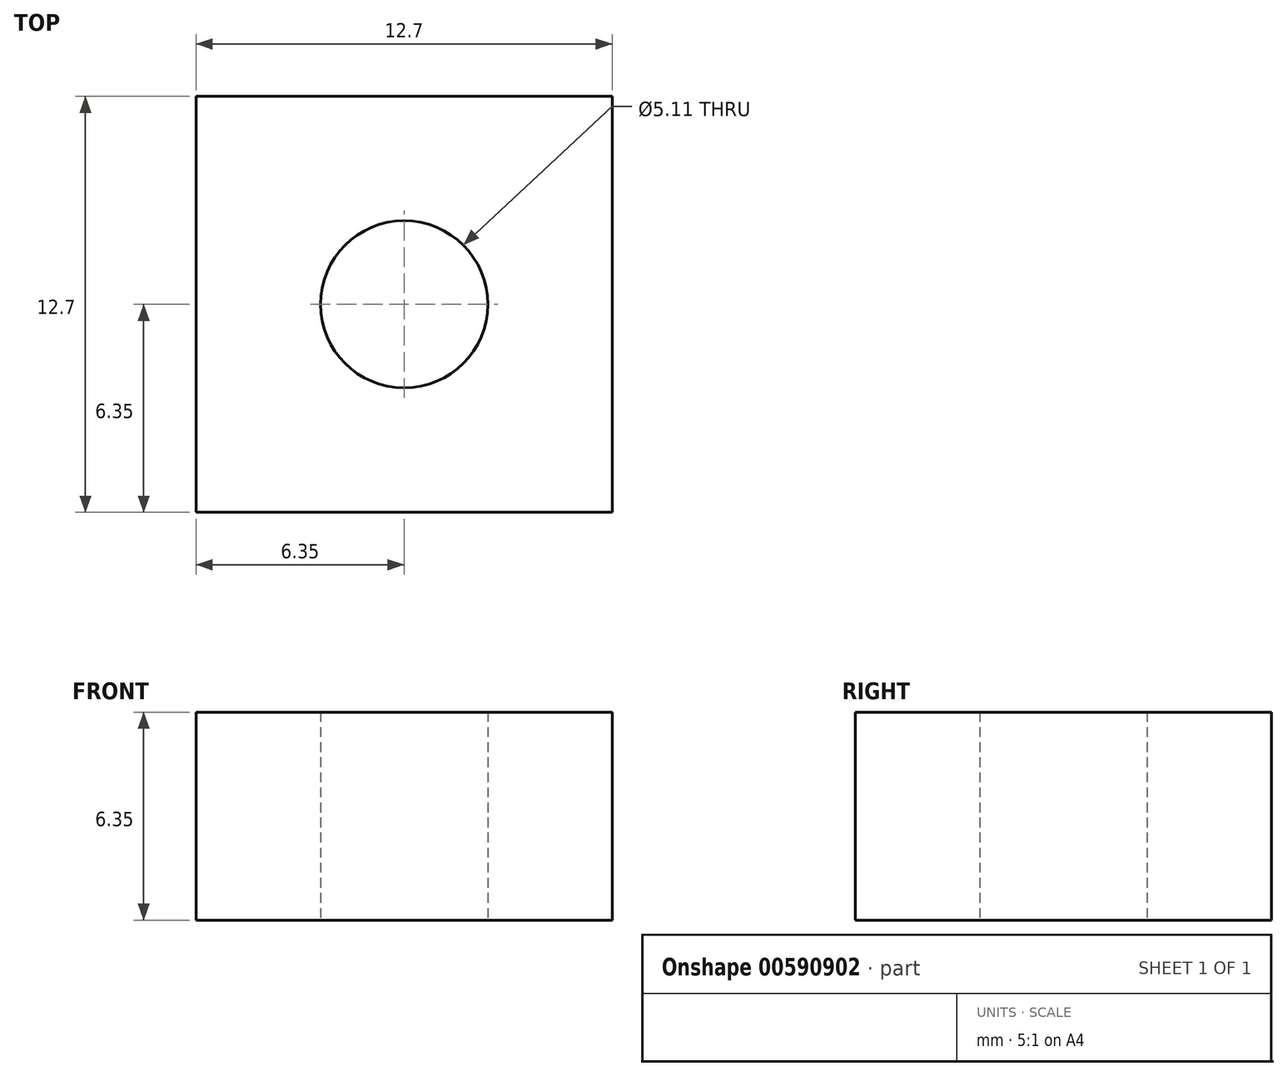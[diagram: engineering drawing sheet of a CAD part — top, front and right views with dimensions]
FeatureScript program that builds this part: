
annotation { "Feature Type Name" : "Feature", "Feature Type Description" : "" }
export const myFeature = defineFeature(function(context is Context, id is Id, definition is map)
    precondition{}
    {
        {
            var Q0;
            Q0=qCreatedBy(makeId("Top.planeOp"),FACE);
            var sketch = newSketch(context, id + "F0", { "sketchPlane" : qUnion([Q0])});
            skLineSegment(sketch, "E0.bottom", {"start": v(6.35, 6.35) * mm, "end": v(-6.35, 6.35) * mm});
            skLineSegment(sketch, "E0.top", {"start": v(6.35, -6.35) * mm, "end": v(-6.35, -6.35) * mm});
            skLineSegment(sketch, "E0.left", {"start": v(6.35, 6.35) * mm, "end": v(6.35, -6.35) * mm});
            skLineSegment(sketch, "E0.right", {"start": v(-6.35, 6.35) * mm, "end": v(-6.35, -6.35) * mm});
            skPoint(sketch, "E0.middle", {"position": v(0, 0) * mm});
            skSolve(sketch);
        }
        {
            var Q0;
            Q0=makeQuery(id+"F0.imprint","IMPRINT",FACE,{"disambiguationData":[TD([[makeQuery(id+"F0.imprint","IMPRINT",EDGE,{"derivedFrom":sQuery(id+"F0.wireOp",EDGE,"E0.bottom")}),1.0]])]});
            extrude(context, id + "F1", {"entities" : qUnion([Q0]), "depth" : 6.35 * mm, "offsetDistance" : 25.4 * mm});
        }
        {
            var Q0;
            Q0=sQuery(id+"F0.wireOp",VERTEX,"E0.middle");
            var Q1;
            Q1=makeQuery(id+"F1.opExtrude","SWEPT_BODY",BODY,{"disambiguationData":[OSD([sQuery(id+"F0.wireOp",EDGE,"E0.bottom"),sQuery(id+"F0.wireOp",EDGE,"E0.top"),sQuery(id+"F0.wireOp",EDGE,"E0.left"),sQuery(id+"F0.wireOp",EDGE,"E0.right")])]});
            hole(context, id + "F2", {"style" : HoleStyle.SIMPLE, "endStyle" : HoleEndStyle.BLIND, "oppositeDirection" : true, "standardTappedOrClearance" : lookupTablePath({ "standard" : "ANSI", "engagement" : "75%", "pitch" : "20 tpi", "size" : "1/4", "type" : "Tapped" }), "standardBlindInLast" : lookupTablePath({ "standard" : "ANSI", "engagement" : "75%", "pitch" : "20 tpi", "size" : "1/4", "type" : "Tapped" }), "holeDiameter" : 5.1 * mm, "majorDiameter" : 6.35 * mm, "showTappedDepth" : true, "holeDepth" : 16.51 * mm, "isTappedThrough" : true, "tappedDepth" : 12.7 * mm, "tapClearance" : 3, "startFromSketch" : true, "locations" : qUnion([Q0]), "scope" : qUnion([Q1])});
        }
    });
